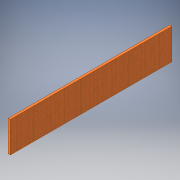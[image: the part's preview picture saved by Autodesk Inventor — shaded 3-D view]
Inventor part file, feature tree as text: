
AUTODESK INVENTOR PART (.ipt)
format: ipt  version: 2016 (Build 200138000, 138)  size: 102,400 bytes
history: native  units: in
note: dims shown in document units (in); Inventor stores cm internally (conversion verified against a paired STEP export)
features: extrude x1, sketch x1
ambient origin geometry x8: Origin, YZ Plane, XZ Plane, XY Plane, X Axis, Y Axis, Z Axis, Center Point
bodies: Solid1 (feature_tree)
feature tree (2):
  extrude  "Extrusion1"  Depth=6.5in
  sketch  "Sketch1"  dims[d0=34.0in d1=6.5in d2=0.4375in d3=0.0in]
